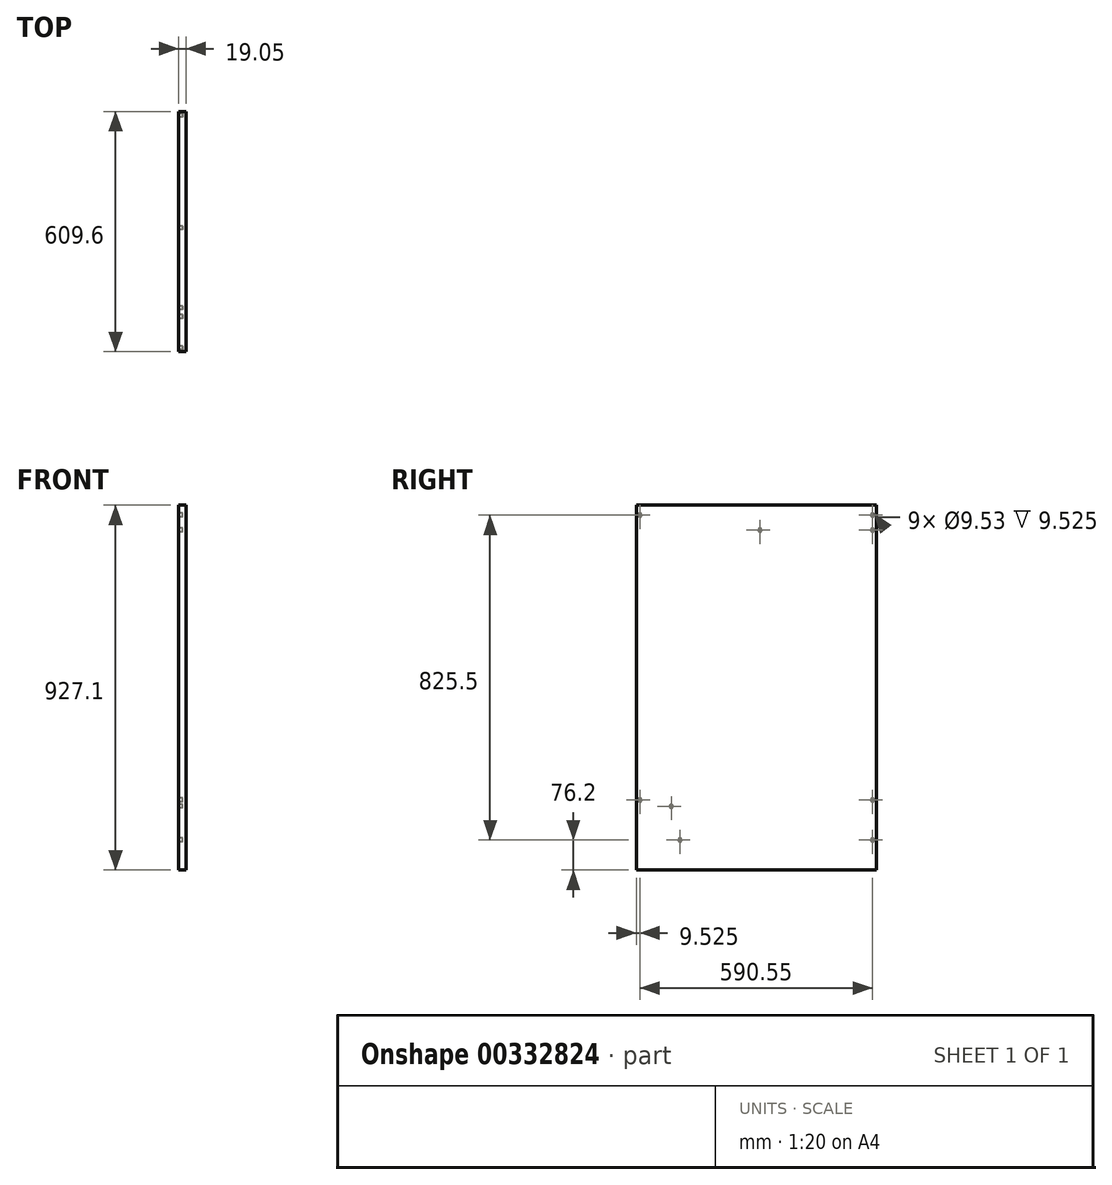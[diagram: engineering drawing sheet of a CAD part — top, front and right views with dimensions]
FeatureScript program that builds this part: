
annotation { "Feature Type Name" : "Feature", "Feature Type Description" : "" }
export const myFeature = defineFeature(function(context is Context, id is Id, definition is map)
    precondition{}
    {
        {
            var Q0;
            Q0=qCreatedBy(makeId("Right.planeOp"),FACE);
            var sketch = newSketch(context, id + "F0", { "sketchPlane" : qUnion([Q0])});
            skLineSegment(sketch, "E0.bottom", {"start": v(0, 0) * mm, "end": v(-609.6, 0) * mm});
            skLineSegment(sketch, "E0.top", {"start": v(0, 927.1) * mm, "end": v(-609.6, 927.1) * mm});
            skLineSegment(sketch, "E0.left", {"start": v(0, 0) * mm, "end": v(0, 927.1) * mm});
            skLineSegment(sketch, "E0.right", {"start": v(-609.6, 0) * mm, "end": v(-609.6, 927.1) * mm});
            skSolve(sketch);
        }
        {
            var Q0;
            Q0=qSketchRegion(id+"F0",true);
            extrude(context, id + "F1", {"entities" : qUnion([Q0]), "depth" : 19.05 * mm});
        }
        {
            var Q0;
            Q0=qCreatedBy(makeId("Right.planeOp"),FACE);
            cPlane(context, id + "F2", {"entities" : qUnion([Q0]), "cplaneType" : CPlaneType.OFFSET, "offset" : 25.4 * mm, "oppositeDirection" : true, "width" : 152.4 * mm, "height" : 152.4 * mm});
        }
        {
            var Q0;
            Q0=qCreatedBy(id+"F2.planeOp",FACE);
            var sketch = newSketch(context, id + "F3", { "sketchPlane" : qUnion([Q0])});
            skCircle(sketch, "E1", {"center": v(-536.58, 63.5) * mm, "radius": 4.76 * mm, "construction": true});
            skCircle(sketch, "E2", {"center": v(-9.52, 76.2) * mm, "radius": 4.76 * mm});
            skCircle(sketch, "E3", {"center": v(-536.58, 177.8) * mm, "radius": 4.76 * mm, "construction": true});
            skCircle(sketch, "E4", {"center": v(-600.08, 177.8) * mm, "radius": 4.76 * mm});
            skCircle(sketch, "E5", {"center": v(-600.07, 901.7) * mm, "radius": 4.76 * mm});
            skCircle(sketch, "E6", {"center": v(-295.28, 1365.25) * mm, "radius": 4.76 * mm});
            skCircle(sketch, "E7", {"center": v(-295.28, 2089.15) * mm, "radius": 4.76 * mm});
            skCircle(sketch, "E8", {"center": v(-295.27, 863.6) * mm, "radius": 4.76 * mm});
            skCircle(sketch, "E9", {"center": v(-9.52, 863.6) * mm, "radius": 4.76 * mm});
            skCircle(sketch, "E10", {"center": v(-9.53, 2089.15) * mm, "radius": 4.76 * mm});
            skCircle(sketch, "E11", {"center": v(-9.53, 1365.25) * mm, "radius": 4.76 * mm});
            skCircle(sketch, "E12", {"center": v(-9.53, 901.7) * mm, "radius": 4.76 * mm});
            skCircle(sketch, "E13", {"center": v(-9.53, 177.8) * mm, "radius": 4.76 * mm});
            skCircle(sketch, "E14", {"center": v(-498.48, 76.2) * mm, "radius": 4.76 * mm});
            skCircle(sketch, "E15", {"center": v(-520.7, 161.93) * mm, "radius": 4.76 * mm});
            skSolve(sketch);
        }
        {
            var Q0;
            Q0=qSketchRegion(id+"F3",true);
            extrude(context, id + "F4", {"entities" : qUnion([Q0]), "operationType" : NewBodyOperationType.REMOVE, "depth" : 34.92 * mm});
        }
    });
